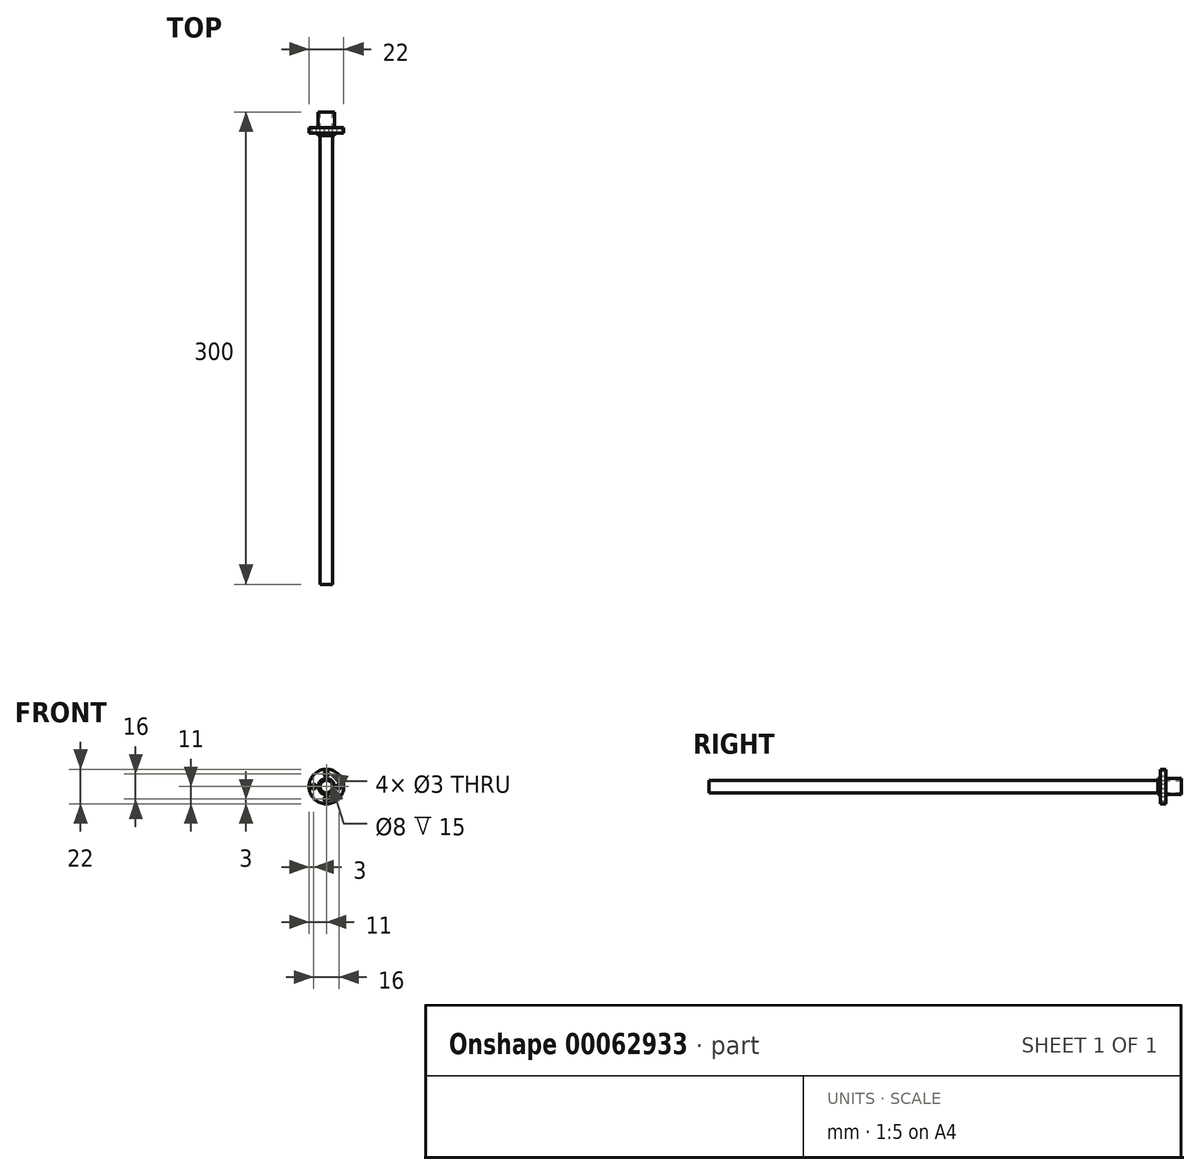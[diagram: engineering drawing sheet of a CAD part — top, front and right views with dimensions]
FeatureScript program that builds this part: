
annotation { "Feature Type Name" : "Feature", "Feature Type Description" : "" }
export const myFeature = defineFeature(function(context is Context, id is Id, definition is map)
    precondition{}
    {
        {
            var Q0;
            Q0=qCreatedBy(makeId("Front.planeOp"),FACE);
            var sketch = newSketch(context, id + "F0", { "sketchPlane" : qUnion([Q0])});
            skCircle(sketch, "E0", {"center": v(0, 0) * mm, "radius": 4 * mm});
            skSolve(sketch);
        }
        {
            var Q0;
            Q0 = qSketchRegion(id + "F0", true);
            extrude(context, id + "F1", {"entities" : qUnion([Q0]), "depth" : 300 * mm});
        }
        {
            var Q0;
            Q0=qCreatedBy(makeId("Front.planeOp"),FACE);
            var sketch = newSketch(context, id + "F2", { "sketchPlane" : qUnion([Q0])});
            skCircle(sketch, "E1", {"center": v(0, 0) * mm, "radius": 5.1 * mm});
            skCircle(sketch, "E2", {"center": v(0, 0) * mm, "radius": 4 * mm});
            skSolve(sketch);
        }
        {
            var Q0;
            Q0 = qSketchRegion(id + "F2", true);
            extrude(context, id + "F3", {"entities" : qUnion([Q0]), "depth" : 15 * mm});
        }
        {
            var Q0;
            Q0=makeQuery(id+"F3.opExtrude","CAP_FACE",FACE,{"disambiguationData":[OSD([sQuery(id+"F2.wireOp",EDGE,"E1"),sQuery(id+"F2.wireOp",EDGE,"E2")])],"isStart":false});
            cPlane(context, id + "F4", {"entities" : qUnion([Q0]), "cplaneType" : CPlaneType.OFFSET, "offset" : 1.5 * mm, "oppositeDirection" : true, "width" : 150 * mm, "height" : 150 * mm});
        }
        {
            var Q0;
            Q0=qCreatedBy(id+"F4.planeOp",FACE);
            var sketch = newSketch(context, id + "F5", { "sketchPlane" : qUnion([Q0])});
            skCircle(sketch, "E3", {"center": v(0, 0) * mm, "radius": 11 * mm});
            skCircle(sketch, "E4", {"center": v(0, 0) * mm, "radius": 5.1 * mm});
            skCircle(sketch, "E5", {"center": v(0, 0) * mm, "radius": 8 * mm, "construction": true});
            skCircle(sketch, "E6", {"center": v(0, 8) * mm, "radius": 1.5 * mm});
            skCircle(sketch, "E7", {"center": v(-8, 0) * mm, "radius": 1.5 * mm});
            skCircle(sketch, "E8", {"center": v(8, 0) * mm, "radius": 1.5 * mm});
            skCircle(sketch, "E9", {"center": v(0, -8) * mm, "radius": 1.5 * mm});
            skSolve(sketch);
        }
        {
            var Q0;
            Q0 = qSketchRegion(id + "F5", true);
            extrude(context, id + "F6", {"entities" : qUnion([Q0]), "operationType" : NewBodyOperationType.ADD, "oppositeDirection" : true, "depth" : 3.5 * mm});
        }
    });
